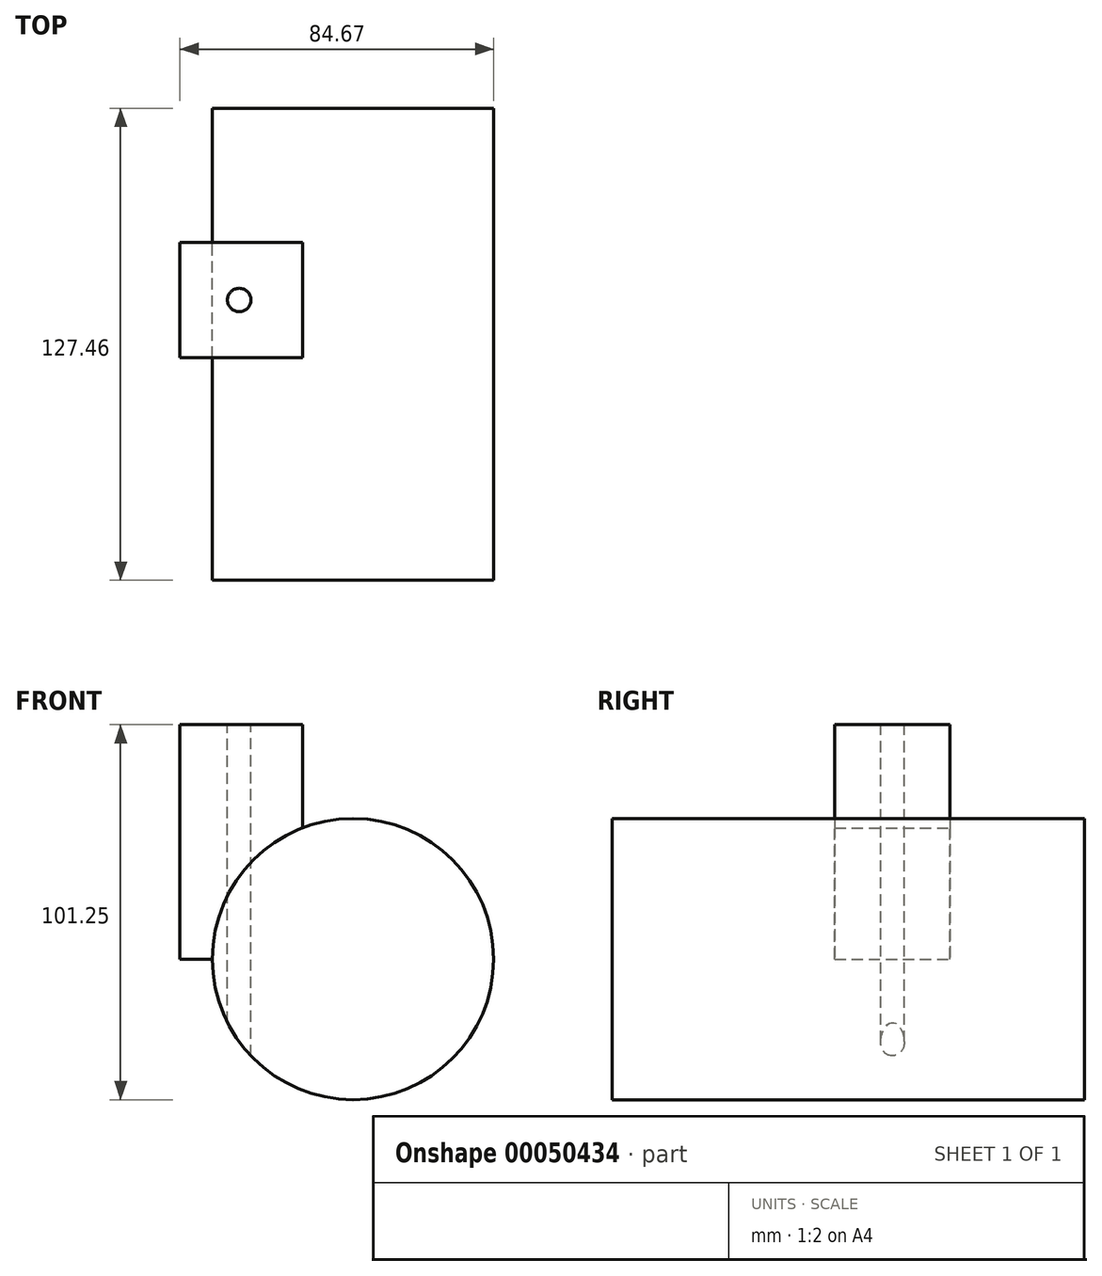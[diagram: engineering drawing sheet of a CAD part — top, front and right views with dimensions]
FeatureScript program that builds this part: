
annotation { "Feature Type Name" : "Feature", "Feature Type Description" : "" }
export const myFeature = defineFeature(function(context is Context, id is Id, definition is map)
    precondition{}
    {
        {
            var Q0;
            Q0=qCreatedBy(makeId("Front.planeOp"),FACE);
            var sketch = newSketch(context, id + "F0", { "sketchPlane" : qUnion([Q0])});
            skCircle(sketch, "E0", {"center": v(0, 0) * mm, "radius": 37.96 * mm});
            skSolve(sketch);
        }
        {
            var Q0;
            Q0=makeQuery(id+"F0.imprint","IMPRINT",FACE,{"disambiguationData":[TD([[makeQuery(id+"F0.imprint","IMPRINT",EDGE,{"derivedFrom":sQuery(id+"F0.wireOp",EDGE,"E0")}),1.0]])]});
            extrude(context, id + "F1", {"entities" : qUnion([Q0]), "depth" : 127.46 * mm});
        }
        {
            var Q0;
            Q0=qCreatedBy(makeId("Top.planeOp"),FACE);
            var sketch = newSketch(context, id + "F2", { "sketchPlane" : qUnion([Q0])});
            skLineSegment(sketch, "E1.bottom", {"start": v(-46.7, -36.21) * mm, "end": v(-13.62, -36.21) * mm});
            skLineSegment(sketch, "E1.top", {"start": v(-46.7, -67.35) * mm, "end": v(-13.62, -67.35) * mm});
            skLineSegment(sketch, "E1.left", {"start": v(-46.7, -36.21) * mm, "end": v(-46.7, -67.35) * mm});
            skLineSegment(sketch, "E1.right", {"start": v(-13.62, -36.21) * mm, "end": v(-13.62, -67.35) * mm});
            skSolve(sketch);
        }
        {
            var Q0;
            Q0=makeQuery(id+"F2.imprint","IMPRINT",FACE,{"disambiguationData":[TD([[makeQuery(id+"F2.imprint","IMPRINT",EDGE,{"derivedFrom":sQuery(id+"F2.wireOp",EDGE,"E1.bottom")}),-1.0]])]});
            extrude(context, id + "F3", {"entities" : qUnion([Q0]), "operationType" : NewBodyOperationType.ADD, "depth" : 63.3 * mm});
        }
        {
            var Q0;
            Q0=makeQuery(id+"F3.opExtrude","CAP_FACE",FACE,{"disambiguationData":[OSD([sQuery(id+"F2.wireOp",EDGE,"E1.bottom"),sQuery(id+"F2.wireOp",EDGE,"E1.top"),sQuery(id+"F2.wireOp",EDGE,"E1.left"),sQuery(id+"F2.wireOp",EDGE,"E1.right")])],"isStart":false});
            var sketch = newSketch(context, id + "F4", { "sketchPlane" : qUnion([Q0])});
            skPoint(sketch, "E2", {"position": v(-30.71, -51.78) * mm});
            skPoint(sketch, "E2.positionSnap0", {"position": v(-13.62, -51.78) * mm});
            skSolve(sketch);
        }
        {
            var Q0;
            Q0=sQuery(id+"F4.wireOp",VERTEX,"E2");
            var Q1;
            Q1=makeQuery(id+"F1.opExtrude","SWEPT_BODY",BODY,{"disambiguationData":[OSD([sQuery(id+"F0.wireOp",EDGE,"E0")])]});
            hole(context, id + "F5", {"style" : HoleStyle.SIMPLE, "holeDiameter" : 6.35 * mm, "endStyle" : HoleEndStyle.THROUGH, "locations" : qUnion([Q0]), "scope" : qUnion([Q1])});
        }
    });
